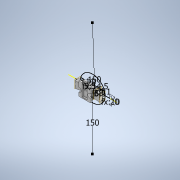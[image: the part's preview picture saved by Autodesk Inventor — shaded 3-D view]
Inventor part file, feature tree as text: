
AUTODESK INVENTOR PART (.ipt)
format: ipt  version: 2020.3 (Build 243373000, 373)  size: 313,344 bytes
history: native  units: mm
features: sketch x9, extrude x6, plane x3, loft x1, mirror x1, fillet x1
ambient origin geometry x8: Origin, YZ Plane, XZ Plane, XY Plane, X Axis, Y Axis, Z Axis, Center Point
bodies: Volumenkörper1 (feature_tree)
feature tree (21):
  sketch  "Skizze1"  dims[d0=68.0mm d1=20.0mm d2=10.0mm d3=5.5mm d4=5.5mm d5=29.0mm d6=14.5mm d8=150.0mm d9=150.0mm]
  extrude  "Extrusion1"  Depth=150.0mm
  extrude  "Extrusion2"  Depth=11.0mm
  sketch  "Skizze3"  dims[d12=14.0mm d13=0.0mm d14=5.0mm]
  plane  "Arbeitsebene1"
  plane  "Arbeitsebene2"
  sketch  "Skizze4"  dims[d15=37.0mm d16=18.5mm]
  plane  "Arbeitsebene3"
  loft  "Erhebung1"
  mirror  "Spiegeln1"
  extrude  "Extrusion4"  Depth=37.0mm
  extrude  "Extrusion5"  Depth=10.0mm TaperAngle=0.0deg
  extrude  "Extrusion3"  Depth=16.0mm
  fillet  "Rundung1"  Radius=8.0mm
  extrude  "Extrusion6"  Depth=10.0mm
  sketch  "Skizze2"  dims[d10=11.0mm d11=11.0mm]
  sketch  "Skizze5"  dims[d17=4.0mm d18=10.0mm d19=0.0mm]
  sketch  "Skizze6"  dims[d20=13.5mm d21=16.0mm d22=8.0mm]
  sketch  "Skizze7"  dims[d24=10.0mm d25=5.0mm]
  sketch  "Skizze8"  dims[d26=0.0mm d27=90.0deg d28=0.0mm d29=90.0deg]
  sketch  "Skizze9"  dims[d30=11.0mm d31=11.0mm d32=15.75mm d33=0.0mm d34=31.0mm d35=3.6mm d36=15.5mm d37=4.0mm d38=23.5mm d39=11.75mm d40=16.0mm d41=21.0mm d42=16.0mm d43=0.0mm d44=0.0mm d45=14.0mm d46=7.0mm d47=4.0mm d48=34.0mm d49=0.0mm d50=8.0mm d51=4.0mm d52=0.0mm d53=10.0mm d54=5.0mm d55=3.5mm d56=30.5mm d57=2.2mm d58=0.0mm]
